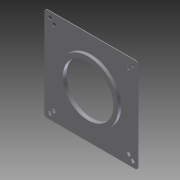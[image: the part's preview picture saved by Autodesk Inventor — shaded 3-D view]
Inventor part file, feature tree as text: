
AUTODESK INVENTOR PART (.ipt)
format: ipt  version: 2011 (Build 150239000, 239)  size: 147,456 bytes
history: native  units: in
note: dims shown in document units (in); Inventor stores cm internally (conversion verified against a paired STEP export)
features: extrude x8, sketch x8, fillet x1
ambient origin geometry x8: Origin, YZ Plane, XZ Plane, XY Plane, X Axis, Y Axis, Z Axis, Center Point
bodies: Solid1 (feature_tree)
feature tree (17):
  extrude  "Extrusion1"  Depth=4.0in
  extrude  "Extrusion2"  Depth=2.16in
  extrude  "Extrusion3"  Depth=1.7655in
  extrude  "Extrusion4"  Depth=0.029in TaperAngle=0.0deg
  extrude  "Extrusion5"  Depth=2.36in
  fillet  "Fillet1"  Radius=2.56in
  extrude  "Extrusion6"  Depth=0.125in
  extrude  "Extrusion7"  Depth=0.131in TaperAngle=0.0deg
  extrude  "Extrusion8"  Depth=0.156in
  sketch  "Sketch1"  dims[d0=4.0in d1=4.0in]
  sketch  "Sketch2"  dims[d2=0.029in d3=0.0in d4=2.16in]
  sketch  "Sketch3"  dims[d5=0.029in d6=0.0in d7=1.7655in]
  sketch  "Sketch4"  dims[d8=0.156in d9=0.029in d10=0.0in]
  sketch  "Sketch5"  dims[d11=0.029in d12=0.0in d13=2.36in d14=2.56in]
  sketch  "Sketch6"  dims[d15=0.262in d16=0.0in d17=0.125in]
  sketch  "Sketch7"  dims[d18=0.131in d19=0.0in d20=0.131in d21=0.0in]
  sketch  "Sketch8"  dims[d22=1.594in d23=0.156in d24=0.131in d25=0.0in]
